# Revit family: Plumbing-Valves-Sloan-ROYAL-BPW-1105
name_source: partatom
category: Plumbing Fixtures
units: mm (PartAtom-declared; Revit-internal decimal feet)

## family parameters
Cut with Voids When Loaded = No
Host = Face
OmniClass Number = 23.45.05.14.99
OmniClass Title = Other Sanitary Washing Plumbing Fixtures
Part Type = Normal
Room Calculation Point = No
Round Connector Dimension = Use Diameter
Shared = No

## types (3) — shared parameters
Assembly Code = D2020300
CW Connection = Yes
Centerline of Supply from Top of Fixture = 26 1/2"
Centerline of Supply to Centerline of Valve = 4 3/4"
Default Elevation = 0"
Edition number = 1
Flush Rate = 1.6 gpf (6.0 Lpf)
HW Connection = No
Height = 26 1/2"
Keynote = 15410
Manufacturer = Sloan Valve
Operating Water Pressure = 15 – 80 PSI (103 – 552 kPa)
Product Material = Sloan Valve - Finish - Polished Chrome
Product data url = https://bimobject.com
URL = www.sloanvalve.com
Valve Pressure Drop = 0.00 psi
Vent Connection = No
Waste Connection = No
Water Inlet Connection Diameter = 1"
zero-valued in all types: CWFU, HWFU, WFU

## per-type parameters (varying)
| type | Description | Part Number |
| ROYAL BPW 1105-1.6 | 1.6 gpf, Polished Chrome Finish, Fixture Connection Top Spud, Single Flush, Royal® Exposed Manual Specialty Water Closet Bedpan Washer
Flushometer. | 3019633 |
| ROYAL BPW 1105-3.5 | 3.5 gpf, Polished Chrome Finish, Fixture Connection Top Spud, Single Flush, Royal® Exposed Manual Specialty Water Closet Bedpan Washer Flushometer. | 3019602 |
| ROYAL BPW 1105-1.6-YI-SG | 1.6 gpf, Double Wall Bumper, Polished Chrome Finish, Fixture Connection Top Spud, Single Flush, Sanigard® Handle, Royal® Exposed Manual Specialty Water Closet Bedpan Washer Flushometer. | 3919600 |

note: column(s) folded — value = type name in every type: Model

## geometry (parser evidence)
native form markers: Sweep x6
no freeform markers — native parametric forms only
